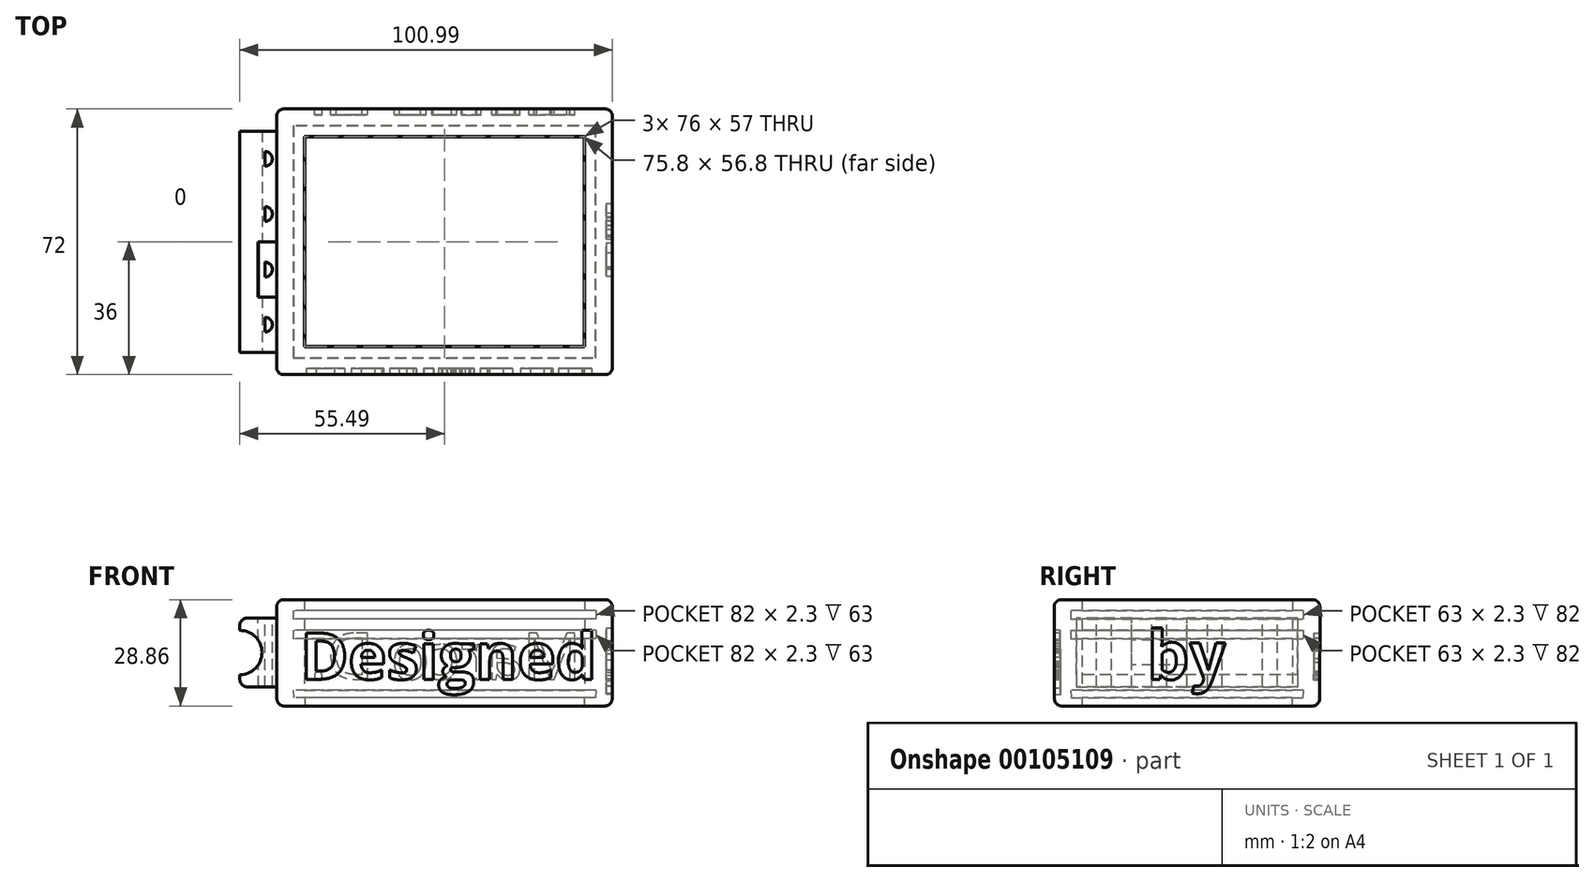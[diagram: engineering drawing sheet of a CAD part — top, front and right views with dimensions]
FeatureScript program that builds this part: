
annotation { "Feature Type Name" : "Feature", "Feature Type Description" : "" }
export const myFeature = defineFeature(function(context is Context, id is Id, definition is map)
    precondition{}
    {
        {
            var Q0;
            Q0=qCreatedBy(makeId("Top.planeOp"),FACE);
            var sketch = newSketch(context, id + "F0", { "sketchPlane" : qUnion([Q0])});
            skPoint(sketch, "E0.middle", {"position": v(0, 0) * mm});
            skLineSegment(sketch, "E1.bottom", {"start": v(0, 0) * mm, "end": v(82, 0) * mm});
            skLineSegment(sketch, "E1.top", {"start": v(0, -63) * mm, "end": v(82, -63) * mm});
            skLineSegment(sketch, "E1.left", {"start": v(0, 0) * mm, "end": v(0, -63) * mm});
            skLineSegment(sketch, "E1.right", {"start": v(82, 0) * mm, "end": v(82, -63) * mm});
            skSolve(sketch);
        }
        {
            var Q0;
            Q0=qCreatedBy(makeId("Front.planeOp"),FACE);
            var sketch = newSketch(context, id + "F1", { "sketchPlane" : qUnion([Q0])});
            skLineSegment(sketch, "E2", {"start": v(3, 0) * mm, "end": v(0, 0) * mm});
            skLineSegment(sketch, "E3", {"start": v(0, 0) * mm, "end": v(0.1, -2) * mm});
            skLineSegment(sketch, "E4", {"start": v(0.1, -2) * mm, "end": v(3.1, -2) * mm});
            skLineSegment(sketch, "E5", {"start": v(3, 16.3) * mm, "end": v(0, 16.3) * mm});
            skLineSegment(sketch, "E6", {"start": v(0, 16.3) * mm, "end": v(0, 14) * mm});
            skLineSegment(sketch, "E7", {"start": v(0, 14) * mm, "end": v(3, 14) * mm});
            skLineSegment(sketch, "E8", {"start": v(3, 19.3) * mm, "end": v(0, 19.3) * mm});
            skLineSegment(sketch, "E9", {"start": v(0, 19.3) * mm, "end": v(0, 21.6) * mm});
            skLineSegment(sketch, "E10", {"start": v(0, 21.6) * mm, "end": v(3, 21.6) * mm});
            skLineSegment(sketch, "E11", {"start": v(3, 21.6) * mm, "end": v(3, 24.6) * mm});
            skLineSegment(sketch, "E12", {"start": v(3, 24.6) * mm, "end": v(-4.51, 24.6) * mm});
            skLineSegment(sketch, "E13", {"start": v(3.1, -2) * mm, "end": v(3.1, -4.26) * mm});
            skLineSegment(sketch, "E14", {"start": v(3.1, -4.26) * mm, "end": v(-4.41, -4.26) * mm});
            skLineSegment(sketch, "E15", {"start": v(3, 19.3) * mm, "end": v(3, 16.3) * mm});
            skLineSegment(sketch, "E16", {"start": v(3, 14) * mm, "end": v(3, 0) * mm});
            skLineSegment(sketch, "E17", {"start": v(-4.51, 24.6) * mm, "end": v(-4.41, -4.26) * mm});
            skSolve(sketch);
        }
        {
            var Q0;
            Q0=qSketchRegion(id+"F1",true);
            var Q1;
            Q1=qConstructionFilter(qBodyType(qCreatedBy(id+"F0",EDGE),BodyType.WIRE),ConstructionObject.NO);
            sweep(context, id + "F2", {"profiles" : qUnion([Q0]), "path" : qUnion([Q1])});
        }
        {
            var Q0;
            Q0=makeQuery(id+"F2.opSweep","MID_CAP_EDGE",EDGE,{"disambiguationData":[OSD([sQuery(id+"F0.wireOp",VERTEX,"E1.left.end"),sQuery(id+"F1.wireOp",EDGE,"E17")])],"capPos":1.0});
            var Q1;
            Q1=makeQuery(id+"F2.opSweep","SWEPT_EDGE",EDGE,{"disambiguationData":[OSD([sQuery(id+"F0.wireOp",EDGE,"E1.top"),sQuery(id+"F1.wireOp",EDGE,"E12"),sQuery(id+"F1.wireOp",EDGE,"E17")])]});
            var Q2;
            Q2=makeQuery(id+"F2.opSweep","SWEPT_EDGE",EDGE,{"disambiguationData":[OSD([sQuery(id+"F0.wireOp",EDGE,"E1.left"),sQuery(id+"F1.wireOp",EDGE,"E12"),sQuery(id+"F1.wireOp",EDGE,"E17")])]});
            var Q3;
            Q3=makeQuery(id+"F2.opSweep","SWEPT_FACE",FACE,{"disambiguationData":[OSD([sQuery(id+"F0.wireOp",EDGE,"E1.left"),sQuery(id+"F1.wireOp",EDGE,"E17")])]});
            var Q4;
            Q4=makeQuery(id+"F2.opSweep","SWEPT_FACE",FACE,{"disambiguationData":[OSD([sQuery(id+"F0.wireOp",EDGE,"E1.top"),sQuery(id+"F1.wireOp",EDGE,"E17")])]});
            var Q5;
            Q5=makeQuery(id+"F2.opSweep","SWEPT_FACE",FACE,{"disambiguationData":[OSD([sQuery(id+"F0.wireOp",EDGE,"E1.bottom"),sQuery(id+"F1.wireOp",EDGE,"E17")])]});
            var Q6;
            Q6=makeQuery(id+"F2.opSweep","SWEPT_FACE",FACE,{"disambiguationData":[OSD([sQuery(id+"F0.wireOp",EDGE,"E1.right"),sQuery(id+"F1.wireOp",EDGE,"E17")])]});
            fillet(context, id + "F3", {"entities" : qUnion([Q0, Q1, Q2, Q3, Q4, Q5, Q6]), "radius" : 2 * mm, "tangentPropagation" : true, "allowEdgeOverflow" : false});
        }
        {
            var Q0;
            Q0=makeQuery(id+"F2.opSweep","SWEPT_FACE",FACE,{"disambiguationData":[OSD([sQuery(id+"F0.wireOp",EDGE,"E1.top"),sQuery(id+"F1.wireOp",EDGE,"E17")])]});
            var sketch = newSketch(context, id + "F4", { "sketchPlane" : qUnion([Q0])});
            skText(sketch, "E18", { "text": "Designed", "fontName": "OpenSans-Bold.ttf"});
            const initialGuessF4  = {"E18": [0.002, 0.00323, 1, 0, 0.01261]};
            skSetInitialGuess(sketch, initialGuessF4);
            skSolve(sketch);
        }
        {
            var Q0;
            Q0=qSketchRegion(id+"F4",true);
            extrude(context, id + "F5", {"entities" : qUnion([Q0]), "operationType" : NewBodyOperationType.REMOVE, "oppositeDirection" : true, "depth" : 1.6 * mm});
        }
        {
            var Q0;
            Q0=makeQuery(id+"F2.opSweep","SWEPT_FACE",FACE,{"disambiguationData":[OSD([sQuery(id+"F0.wireOp",EDGE,"E1.right"),sQuery(id+"F1.wireOp",EDGE,"E17")])]});
            var sketch = newSketch(context, id + "F6", { "sketchPlane" : qUnion([Q0])});
            skText(sketch, "E19", { "text": "by", "fontName": "NotoSansCJKsc-Bold.otf"});
            skPoint(sketch, "E20.endSnap0", {"position": v(-65.46, 10.46) * mm});
            const initialGuessF6  = {"E19": [-0.04224, 0.0033, 1, 0, 0.0126]};
            skSetInitialGuess(sketch, initialGuessF6);
            skSolve(sketch);
        }
        {
            var Q0;
            Q0=qSketchRegion(id+"F6",true);
            extrude(context, id + "F7", {"entities" : qUnion([Q0]), "operationType" : NewBodyOperationType.REMOVE, "oppositeDirection" : true, "depth" : 1.6 * mm});
        }
        {
            var Q0;
            Q0=makeQuery(id+"F2.opSweep","SWEPT_FACE",FACE,{"disambiguationData":[OSD([sQuery(id+"F0.wireOp",EDGE,"E1.bottom"),sQuery(id+"F1.wireOp",EDGE,"E17")])]});
            var sketch = newSketch(context, id + "F8", { "sketchPlane" : qUnion([Q0])});
            skText(sketch, "E21", { "text": "Marco D.", "fontName": "OpenSans-Regular.ttf"});
            const initialGuessF8  = {"E21": [-0.078, 0.00302, 1, 0, 0.0126]};
            skSetInitialGuess(sketch, initialGuessF8);
            skSolve(sketch);
        }
        {
            var Q0;
            Q0=qSketchRegion(id+"F8",true);
            extrude(context, id + "F9", {"entities" : qUnion([Q0]), "operationType" : NewBodyOperationType.REMOVE, "oppositeDirection" : true, "depth" : 1.6 * mm});
        }
        {
            var Q0;
            Q0=makeQuery(id+"F2.opSweep","SWEPT_FACE",FACE,{"disambiguationData":[OSD([sQuery(id+"F0.wireOp",EDGE,"E1.left"),sQuery(id+"F1.wireOp",EDGE,"E17")])]});
            var sketch = newSketch(context, id + "F10", { "sketchPlane" : qUnion([Q0])});
            skLineSegment(sketch, "E22", {"start": v(31.5, 22.6) * mm, "end": v(31.5, -2.25) * mm});
            skLineSegment(sketch, "E23", {"start": v(65.46, 10.18) * mm, "end": v(31.5, 10.3) * mm});
            skLineSegment(sketch, "E24.bottom", {"start": v(1.5, 19.6) * mm, "end": v(61.5, 19.6) * mm});
            skLineSegment(sketch, "E24.top", {"start": v(1.5, 0.98) * mm, "end": v(61.5, 0.98) * mm});
            skLineSegment(sketch, "E24.left", {"start": v(1.5, 19.6) * mm, "end": v(1.5, 0.98) * mm});
            skLineSegment(sketch, "E24.right", {"start": v(61.5, 19.6) * mm, "end": v(61.5, 0.98) * mm});
            skPoint(sketch, "E24.middle", {"position": v(31.5, 10.3) * mm});
            skSolve(sketch);
        }
        {
            var Q0;
            Q0 = qSketchRegion(id + "F10", true);
            extrude(context, id + "F11", {"entities" : qUnion([Q0]), "operationType" : NewBodyOperationType.ADD, "depth" : 10 * mm});
        }
        {
            var Q0;
            Q0=makeQuery(id+"F11.opExtrude","SWEPT_FACE",FACE,{"disambiguationData":[OSD([sQuery(id+"F10.wireOp",EDGE,"E24.right")])]});
            var sketch = newSketch(context, id + "F12", { "sketchPlane" : qUnion([Q0])});
            skArc(sketch, "E25", {"start": v(-14.44, 4.24) * mm, "mid": v(-8.46, 10.26) * mm, "end": v(-14.48, 16.24) * mm});
            skLineSegment(sketch, "E26", {"start": v(-4.46, 10.28) * mm, "end": v(-14.46, 10.24) * mm});
            skSolve(sketch);
        }
        {
            var Q0;
            {var subQ0=sQuery(id+"F12.wireOp",EDGE,"E25");var subQ1=makeQuery(id+"F11.opExtrude","CAP_EDGE",EDGE,{"disambiguationData":[OSD([sQuery(id+"F10.wireOp",EDGE,"E24.right")])],"isStart":false});var subQ2=makeQuery(id+"F12.imprint","INTERSECT",VERTEX,{"disambiguationData":[OD(0.0)],"derivedFrom":[subQ1,subQ0]});Q0=makeQuery(id+"F12.imprint","IMPRINT",FACE,{"disambiguationData":[TD([[makeQuery(id+"F12.imprint","IMPRINT",EDGE,{"disambiguationData":[TD([[subQ2,-1.0]])],"derivedFrom":subQ0}),1.0]])]});}
            var Q1;
            {var subQ0=sQuery(id+"F12.wireOp",EDGE,"E25");var subQ1=makeQuery(id+"F11.opExtrude","CAP_EDGE",EDGE,{"disambiguationData":[OSD([sQuery(id+"F10.wireOp",EDGE,"E24.right")])],"isStart":false});var subQ2=makeQuery(id+"F12.imprint","INTERSECT",VERTEX,{"disambiguationData":[OD(1.0)],"derivedFrom":[subQ1,subQ0]});Q1=makeQuery(id+"F12.imprint","IMPRINT",FACE,{"disambiguationData":[TD([[makeQuery(id+"F12.imprint","IMPRINT",EDGE,{"disambiguationData":[TD([[subQ2,1.0]])],"derivedFrom":subQ0}),1.0]])]});}
            extrude(context, id + "F13", {"entities" : qUnion([Q0, Q1]), "operationType" : NewBodyOperationType.REMOVE, "endBound" : BoundingType.UP_TO_NEXT, "oppositeDirection" : true, "depth" : 25 * mm});
        }
        {
            var Q0;
            Q0=makeQuery(id+"F11.opExtrude","SWEPT_FACE",FACE,{"disambiguationData":[OSD([sQuery(id+"F10.wireOp",EDGE,"E24.bottom")])]});
            var sketch = newSketch(context, id + "F14", { "sketchPlane" : qUnion([Q0])});
            skLineSegment(sketch, "E27", {"start": v(-9.43, -61.5) * mm, "end": v(-9.43, -1.5) * mm});
            skLineSegment(sketch, "E28", {"start": v(-14.43, -31.5) * mm, "end": v(-4.43, -31.5) * mm});
            skLineSegment(sketch, "E29", {"start": v(-12.3, -31.5) * mm, "end": v(-12.3, -61.5) * mm});
            skLineSegment(sketch, "E30", {"start": v(-12.3, -46.5) * mm, "end": v(-4.43, -46.5) * mm});
            skLineSegment(sketch, "E31", {"start": v(-7.6, -55.97) * mm, "end": v(-7.6, -51.97) * mm});
            skArc(sketch, "E32", {"start": v(-7.6, -55.97) * mm, "mid": v(-5.6, -53.97) * mm, "end": v(-7.6, -51.97) * mm});
            skArc(sketch, "E33.MirrorCS", {"start": v(-7.6, -37.03) * mm, "mid": v(-5.6, -39.03) * mm, "end": v(-7.6, -41.03) * mm});
            skLineSegment(sketch, "E34.MirrorCS", {"start": v(-7.6, -37.03) * mm, "end": v(-7.6, -41.03) * mm});
            skArc(sketch, "E35.MirrorCS", {"start": v(-7.6, -25.97) * mm, "mid": v(-5.6, -23.97) * mm, "end": v(-7.6, -21.97) * mm});
            skLineSegment(sketch, "E36.MirrorCS", {"start": v(-7.6, -25.97) * mm, "end": v(-7.6, -21.97) * mm});
            skLineSegment(sketch, "E37.MirrorCS", {"start": v(-7.6, -7.03) * mm, "end": v(-7.6, -11.03) * mm});
            skArc(sketch, "E38.MirrorCS", {"start": v(-7.6, -7.03) * mm, "mid": v(-5.6, -9.03) * mm, "end": v(-7.6, -11.03) * mm});
            skSolve(sketch);
        }
        {
            var Q0;
            Q0=makeQuery(id+"F14.imprint","IMPRINT",FACE,{"disambiguationData":[TD([[makeQuery(id+"F14.imprint","IMPRINT",EDGE,{"derivedFrom":sQuery(id+"F14.wireOp",EDGE,"E31")}),-1.0]])]});
            var Q1;
            Q1=makeQuery(id+"F14.imprint","IMPRINT",FACE,{"disambiguationData":[TD([[makeQuery(id+"F14.imprint","IMPRINT",EDGE,{"derivedFrom":sQuery(id+"F14.wireOp",EDGE,"E33.MirrorCS")}),-1.0]])]});
            var Q2;
            Q2=makeQuery(id+"F14.imprint","IMPRINT",FACE,{"disambiguationData":[TD([[makeQuery(id+"F14.imprint","IMPRINT",EDGE,{"derivedFrom":sQuery(id+"F14.wireOp",EDGE,"E35.MirrorCS")}),1.0]])]});
            var Q3;
            Q3=makeQuery(id+"F14.imprint","IMPRINT",FACE,{"disambiguationData":[TD([[makeQuery(id+"F14.imprint","IMPRINT",EDGE,{"derivedFrom":sQuery(id+"F14.wireOp",EDGE,"E37.MirrorCS")}),1.0]])]});
            extrude(context, id + "F15", {"entities" : qUnion([Q0, Q1, Q2, Q3]), "operationType" : NewBodyOperationType.REMOVE, "endBound" : BoundingType.UP_TO_NEXT, "oppositeDirection" : true, "depth" : 25 * mm});
        }
        {
            var Q0;
            Q0=makeQuery(id+"F11.opExtrude","CAP_EDGE",EDGE,{"disambiguationData":[OSD([sQuery(id+"F10.wireOp",EDGE,"E24.bottom")])],"isStart":true});
            var Q1;
            Q1=makeQuery(id+"F11.opExtrude","CAP_EDGE",EDGE,{"disambiguationData":[OSD([sQuery(id+"F10.wireOp",EDGE,"E24.right")])],"isStart":true});
            var Q2;
            Q2=makeQuery(id+"F11.opExtrude","CAP_EDGE",EDGE,{"disambiguationData":[OSD([sQuery(id+"F10.wireOp",EDGE,"E24.top")])],"isStart":true});
            var Q3;
            Q3=makeQuery(id+"F11.opExtrude","CAP_EDGE",EDGE,{"disambiguationData":[OSD([sQuery(id+"F10.wireOp",EDGE,"E24.left")])],"isStart":true});
            var Q4;
            Q4=makeQuery(id+"F11.opExtrude","CAP_EDGE",EDGE,{"disambiguationData":[OSD([sQuery(id+"F10.wireOp",EDGE,"E24.top")])],"isStart":false});
            var Q5;
            Q5=makeQuery(id+"F11.opExtrude","CAP_EDGE",EDGE,{"disambiguationData":[OSD([sQuery(id+"F10.wireOp",EDGE,"E24.bottom")])],"isStart":false});
            fillet(context, id + "F16", {"entities" : qUnion([Q0, Q1, Q2, Q3, Q4, Q5]), "radius" : 2 * mm, "tangentPropagation" : true, "allowEdgeOverflow" : false});
        }
    });
